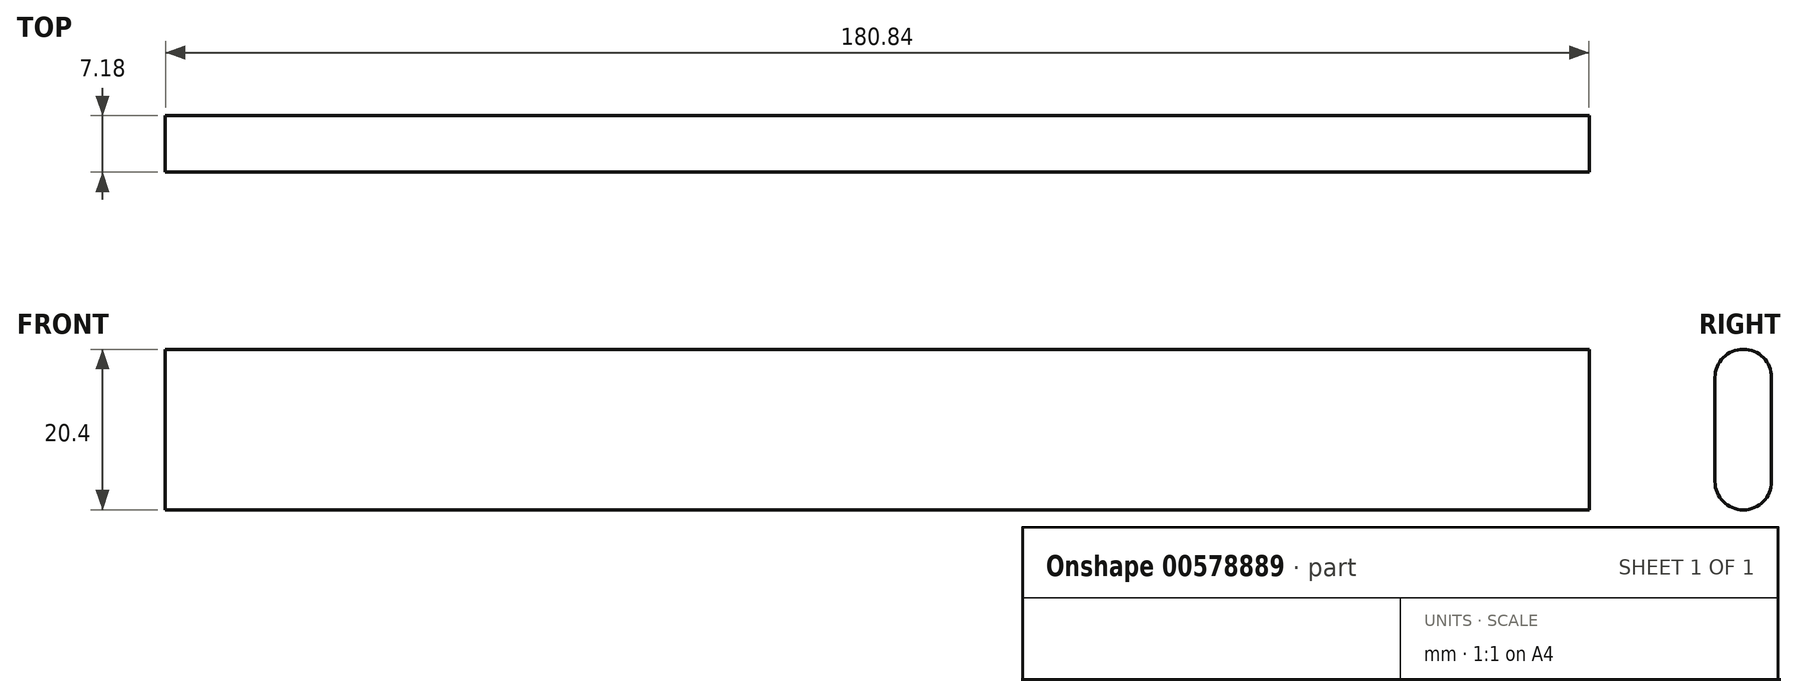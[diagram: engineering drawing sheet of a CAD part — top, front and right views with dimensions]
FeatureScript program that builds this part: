
annotation { "Feature Type Name" : "Feature", "Feature Type Description" : "" }
export const myFeature = defineFeature(function(context is Context, id is Id, definition is map)
    precondition{}
    {
        {
            var Q0;
            Q0=qCreatedBy(makeId("Right.planeOp"),FACE);
            var sketch = newSketch(context, id + "F0", { "sketchPlane" : qUnion([Q0])});
            skLineSegment(sketch, "E0.rect.left", {"start": v(3.6, 6.6) * mm, "end": v(3.6, -6.6) * mm});
            skLineSegment(sketch, "E0.rect.right", {"start": v(-3.6, 6.6) * mm, "end": v(-3.6, -6.6) * mm});
            skPoint(sketch, "E0.rect.middle", {"position": v(0, 0) * mm});
            skArc(sketch, "E1", {"start": v(3.6, 6.6) * mm, "mid": v(0, 10.2) * mm, "end": v(-3.6, 6.6) * mm});
            skArc(sketch, "E2", {"start": v(-3.6, -6.6) * mm, "mid": v(0, -10.2) * mm, "end": v(3.6, -6.6) * mm});
            skSolve(sketch);
        }
        {
            var Q0;
            Q0=qSketchRegion(id+"F0",true);
            extrude(context, id + "F1", {"entities" : qUnion([Q0]), "endBound" : BoundingType.SYMMETRIC, "depth" : 180.85 * mm});
        }
    });
